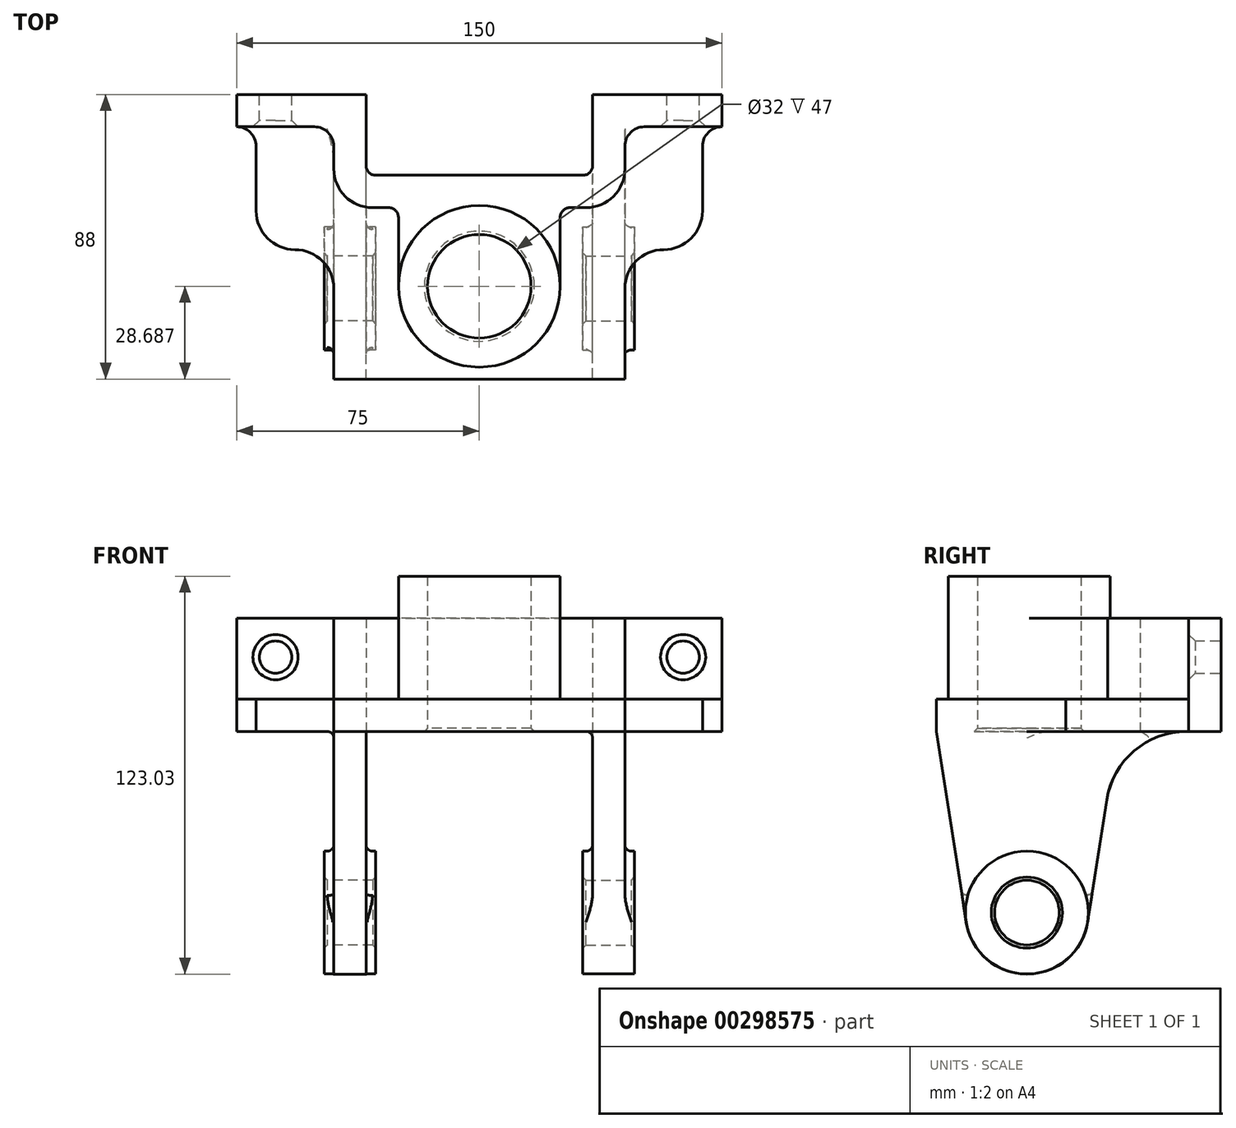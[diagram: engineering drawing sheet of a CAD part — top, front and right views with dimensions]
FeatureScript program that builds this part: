
annotation { "Feature Type Name" : "Feature", "Feature Type Description" : "" }
export const myFeature = defineFeature(function(context is Context, id is Id, definition is map)
    precondition{}
    {
        {
            var Q0;
            Q0=qCreatedBy(makeId("Top.planeOp"),FACE);
            var sketch = newSketch(context, id + "F0", { "sketchPlane" : qUnion([Q0])});
            skLineSegment(sketch, "E0", {"start": v(0, 0) * mm, "end": v(32, 0) * mm});
            skLineSegment(sketch, "E1", {"start": v(35, 3) * mm, "end": v(35, 25) * mm});
            skLineSegment(sketch, "E2", {"start": v(35, 25) * mm, "end": v(75, 25) * mm});
            skLineSegment(sketch, "E3", {"start": v(75, 25) * mm, "end": v(75, 15) * mm});
            skLineSegment(sketch, "E4", {"start": v(75, 15) * mm, "end": v(51, 15) * mm});
            skLineSegment(sketch, "E5", {"start": v(45, 9) * mm, "end": v(45, 2) * mm});
            skLineSegment(sketch, "E6", {"start": v(33, -10) * mm, "end": v(25, -10) * mm});
            skLineSegment(sketch, "E7", {"start": v(25, -10) * mm, "end": v(25, -34.31) * mm});
            skArc(sketch, "E8", {"start": v(0, -59.31) * mm, "mid": v(17.68, -52) * mm, "end": v(25, -34.31) * mm});
            skLineSegment(sketch, "E9", {"start": v(0, 0) * mm, "end": v(0, -59.31) * mm});
            skCircle(sketch, "E10", {"center": v(0, -34.31) * mm, "radius": 16 * mm});
            skPoint(sketch, "E11.visualSharp", {"position": v(-35, 0) * mm});
            skPoint(sketch, "E12.visualSharp", {"position": v(35, 0) * mm});
            skArc(sketch, "E12.filletArc", {"start": v(32, 0) * mm, "mid": v(34.12, 0.88) * mm, "end": v(35, 3) * mm});
            skPoint(sketch, "E13.visualSharp", {"position": v(45, -10) * mm});
            skArc(sketch, "E13.filletArc", {"start": v(33, -10) * mm, "mid": v(41.49, -6.49) * mm, "end": v(45, 2) * mm});
            skPoint(sketch, "E14.visualSharp", {"position": v(45, 15) * mm});
            skArc(sketch, "E14.filletArc", {"start": v(51, 15) * mm, "mid": v(46.76, 13.24) * mm, "end": v(45, 9) * mm});
            skPoint(sketch, "E15.MirrorCS.start.orphan", {"position": v(0, 0) * mm});
            skPoint(sketch, "E16.MirrorCS.end.orphan", {"position": v(-35, 25) * mm});
            skPoint(sketch, "E17.MirrorCS.end.orphan", {"position": v(-75, 25) * mm});
            skPoint(sketch, "E18.MirrorCS.end.orphan", {"position": v(-75, 15) * mm});
            skPoint(sketch, "E19.MirrorCS.end.orphan", {"position": v(-45, 15) * mm});
            skPoint(sketch, "E20.MirrorCS.end.orphan", {"position": v(-25, -10) * mm});
            skPoint(sketch, "E21.MirrorCS.end.orphan", {"position": v(-25, -34.31) * mm});
            skPoint(sketch, "E22.MirrorCS.start.orphan", {"position": v(0, -59.31) * mm});
            skLineSegment(sketch, "E23.MirrorCS", {"start": v(0, 0) * mm, "end": v(-32, 0) * mm});
            skArc(sketch, "E24.MirrorCS", {"start": v(-32, 0) * mm, "mid": v(-34.12, 0.88) * mm, "end": v(-35, 3) * mm});
            skLineSegment(sketch, "E25.MirrorCS", {"start": v(-35, 3) * mm, "end": v(-35, 25) * mm});
            skLineSegment(sketch, "E26.MirrorCS", {"start": v(-35, 25) * mm, "end": v(-75, 25) * mm});
            skLineSegment(sketch, "E27.MirrorCS", {"start": v(-75, 25) * mm, "end": v(-75, 15) * mm});
            skArc(sketch, "E28.MirrorCS", {"start": v(-51, 15) * mm, "mid": v(-46.76, 13.24) * mm, "end": v(-45, 9) * mm});
            skLineSegment(sketch, "E29.MirrorCS", {"start": v(-45, 9) * mm, "end": v(-45, 2) * mm});
            skArc(sketch, "E30.MirrorCS", {"start": v(-33, -10) * mm, "mid": v(-41.49, -6.49) * mm, "end": v(-45, 2) * mm});
            skLineSegment(sketch, "E31.MirrorCS", {"start": v(-33, -10) * mm, "end": v(-25, -10) * mm});
            skLineSegment(sketch, "E32.MirrorCS", {"start": v(-25, -10) * mm, "end": v(-25, -34.31) * mm});
            skArc(sketch, "E33.MirrorCS", {"start": v(0, -59.31) * mm, "mid": v(-17.68, -52) * mm, "end": v(-25, -34.31) * mm});
            skLineSegment(sketch, "E34", {"start": v(-51, 15) * mm, "end": v(-75, 15) * mm});
            skSolve(sketch);
        }
        {
            var Q0;
            Q0 = qSketchRegion(id + "F0", true);
            extrude(context, id + "F1", {"entities" : qUnion([Q0]), "depth" : 25 * mm});
        }
        {
            var Q0;
            Q0=makeQuery(id+"F1.opExtrude","CAP_FACE",FACE,{"disambiguationData":[OSD([sQuery(id+"F0.wireOp",EDGE,"E0"),sQuery(id+"F0.wireOp",EDGE,"E1"),sQuery(id+"F0.wireOp",EDGE,"E2"),sQuery(id+"F0.wireOp",EDGE,"E3"),sQuery(id+"F0.wireOp",EDGE,"E4"),sQuery(id+"F0.wireOp",EDGE,"E5"),sQuery(id+"F0.wireOp",EDGE,"E6"),sQuery(id+"F0.wireOp",EDGE,"E7"),sQuery(id+"F0.wireOp",EDGE,"E8"),sQuery(id+"F0.wireOp",EDGE,"E10"),sQuery(id+"F0.wireOp",EDGE,"E12.filletArc"),sQuery(id+"F0.wireOp",EDGE,"E13.filletArc"),sQuery(id+"F0.wireOp",EDGE,"E14.filletArc"),sQuery(id+"F0.wireOp",EDGE,"E23.MirrorCS"),sQuery(id+"F0.wireOp",EDGE,"E24.MirrorCS"),sQuery(id+"F0.wireOp",EDGE,"E25.MirrorCS"),sQuery(id+"F0.wireOp",EDGE,"E26.MirrorCS"),sQuery(id+"F0.wireOp",EDGE,"E27.MirrorCS"),sQuery(id+"F0.wireOp",EDGE,"24cce044-26b0-4711-a261-53512b01c6400.MirrorCS"),sQuery(id+"F0.wireOp",EDGE,"E28.MirrorCS"),sQuery(id+"F0.wireOp",EDGE,"E29.MirrorCS"),sQuery(id+"F0.wireOp",EDGE,"E30.MirrorCS"),sQuery(id+"F0.wireOp",EDGE,"E31.MirrorCS"),sQuery(id+"F0.wireOp",EDGE,"E32.MirrorCS"),sQuery(id+"F0.wireOp",EDGE,"E33.MirrorCS")])],"isStart":false});
            var sketch = newSketch(context, id + "F2", { "sketchPlane" : qUnion([Q0])});
            skCircle(sketch, "E35", {"center": v(0, -34.31) * mm, "radius": 25 * mm});
            skSolve(sketch);
        }
        {
            var Q0;
            Q0 = qSketchRegion(id + "F2", true);
            extrude(context, id + "F3", {"entities" : qUnion([Q0]), "operationType" : NewBodyOperationType.ADD, "depth" : 13 * mm});
        }
        {
            var Q0;
            Q0=makeQuery(id+"F3.opExtrude","CAP_FACE",FACE,{"disambiguationData":[OSD([sQuery(id+"F2.wireOp",EDGE,"E35")])],"isStart":false});
            var sketch = newSketch(context, id + "F4", { "sketchPlane" : qUnion([Q0])});
            skCircle(sketch, "E36", {"center": v(0, -34.31) * mm, "radius": 16 * mm});
            skSolve(sketch);
        }
        {
            var Q0;
            Q0 = qSketchRegion(id + "F4", true);
            extrude(context, id + "F5", {"entities" : qUnion([Q0]), "operationType" : NewBodyOperationType.REMOVE, "endBound" : BoundingType.THROUGH_ALL, "oppositeDirection" : true, "depth" : 25 * mm});
        }
        {
            var Q0;
            Q0=makeQuery(id+"F1.opExtrude","SWEPT_EDGE",EDGE,{"disambiguationData":[OSD([sQuery(id+"F0.wireOp",EDGE,"E6"),sQuery(id+"F0.wireOp",EDGE,"E7")])]});
            var Q1;
            Q1=makeQuery(id+"F1.opExtrude","SWEPT_EDGE",EDGE,{"disambiguationData":[OSD([sQuery(id+"F0.wireOp",EDGE,"E31.MirrorCS"),sQuery(id+"F0.wireOp",EDGE,"E32.MirrorCS")])]});
            fillet(context, id + "F6", {"entities" : qUnion([Q0, Q1]), "radius" : 3 * mm, "tangentPropagation" : true, "allowEdgeOverflow" : false});
        }
        {
            var Q0;
            Q0=qCreatedBy(makeId("Top.planeOp"),FACE);
            var sketch = newSketch(context, id + "F7", { "sketchPlane" : qUnion([Q0])});
            skPoint(sketch, "E37.0", {"position": v(-75, 20) * mm});
            skPoint(sketch, "E38.0", {"position": v(-55, 25) * mm});
            skLineSegment(sketch, "E39.0", {"start": v(-35, 3) * mm, "end": v(-35, 25) * mm});
            skPoint(sketch, "E40.0", {"position": v(-34.12, 0.88) * mm});
            skLineSegment(sketch, "E41.0", {"start": v(-32, 0) * mm, "end": v(32, 0) * mm});
            skPoint(sketch, "E42.0", {"position": v(34.12, 0.88) * mm});
            skLineSegment(sketch, "E43.0", {"start": v(35, 3) * mm, "end": v(35, 25) * mm});
            skLineSegment(sketch, "E44.0", {"start": v(35, 25) * mm, "end": v(75, 25) * mm});
            skLineSegment(sketch, "E45.0.0", {"start": v(75, 15) * mm, "end": v(75, 25) * mm});
            skLineSegment(sketch, "E45.0.2", {"start": v(75, 25) * mm, "end": v(75, 15) * mm});
            skLineSegment(sketch, "E46.0", {"start": v(-35, 25) * mm, "end": v(-75, 25) * mm});
            skArc(sketch, "E47.0", {"start": v(32, 0) * mm, "mid": v(34.12, 0.88) * mm, "end": v(35, 3) * mm});
            skArc(sketch, "E48.0", {"start": v(-32, 0) * mm, "mid": v(-34.12, 0.88) * mm, "end": v(-35, 3) * mm});
            skPoint(sketch, "E49.0.end.orphan", {"position": v(-75, 15) * mm});
            skPoint(sketch, "E49.0.start.orphan", {"position": v(-51, 15) * mm});
            skLineSegment(sketch, "E50.0", {"start": v(-75, 25) * mm, "end": v(-75, 15) * mm});
            skLineSegment(sketch, "E51", {"start": v(75, 15) * mm, "end": v(75, 15) * mm});
            skLineSegment(sketch, "E52", {"start": v(69, 9) * mm, "end": v(69, -11) * mm});
            skLineSegment(sketch, "E53", {"start": v(57, -23) * mm, "end": v(57, -23) * mm});
            skLineSegment(sketch, "E54", {"start": v(45, -35) * mm, "end": v(45, -63) * mm});
            skLineSegment(sketch, "E55", {"start": v(45, -63) * mm, "end": v(-45, -63) * mm});
            skLineSegment(sketch, "E56", {"start": v(-45, -63) * mm, "end": v(-45, -35) * mm});
            skLineSegment(sketch, "E57", {"start": v(-57, -23) * mm, "end": v(-57, -23) * mm});
            skLineSegment(sketch, "E58", {"start": v(-69, -11) * mm, "end": v(-69, 9) * mm});
            skLineSegment(sketch, "E59", {"start": v(-75, 15) * mm, "end": v(-75, 15) * mm});
            skCircle(sketch, "E60.0", {"center": v(0, -34.31) * mm, "radius": 16 * mm});
            skPoint(sketch, "E61.visualSharp", {"position": v(69, 15) * mm});
            skArc(sketch, "E61.filletArc", {"start": v(75, 15) * mm, "mid": v(70.76, 13.24) * mm, "end": v(69, 9) * mm});
            skPoint(sketch, "E62.visualSharp", {"position": v(69, -23) * mm});
            skArc(sketch, "E62.filletArc", {"start": v(57, -23) * mm, "mid": v(65.49, -19.49) * mm, "end": v(69, -11) * mm});
            skPoint(sketch, "E63.visualSharp", {"position": v(45, -23) * mm});
            skArc(sketch, "E63.filletArc", {"start": v(57, -23) * mm, "mid": v(48.51, -26.51) * mm, "end": v(45, -35) * mm});
            skPoint(sketch, "E64.visualSharp", {"position": v(-45, -23) * mm});
            skArc(sketch, "E64.filletArc", {"start": v(-45, -35) * mm, "mid": v(-48.51, -26.51) * mm, "end": v(-57, -23) * mm});
            skPoint(sketch, "E65.visualSharp", {"position": v(-69, -23) * mm});
            skArc(sketch, "E65.filletArc", {"start": v(-69, -11) * mm, "mid": v(-65.49, -19.49) * mm, "end": v(-57, -23) * mm});
            skPoint(sketch, "E66.visualSharp", {"position": v(-69, 15) * mm});
            skArc(sketch, "E66.filletArc", {"start": v(-69, 9) * mm, "mid": v(-70.76, 13.24) * mm, "end": v(-75, 15) * mm});
            skSolve(sketch);
        }
        {
            var Q0;
            Q0 = qSketchRegion(id + "F7", true);
            extrude(context, id + "F8", {"entities" : qUnion([Q0]), "operationType" : NewBodyOperationType.ADD, "oppositeDirection" : true, "depth" : 10 * mm});
        }
        {
            var Q0;
            Q0=makeQuery(id+"F8.opExtrude","SWEPT_FACE",FACE,{"disambiguationData":[OSD([sQuery(id+"F7.wireOp",EDGE,"E54")])]});
            cPlane(context, id + "F9", {"entities" : qUnion([Q0]), "cplaneType" : CPlaneType.OFFSET, "offset" : 0 * mm, "width" : 150 * mm, "height" : 150 * mm});
        }
        {
            var Q0;
            Q0=qCreatedBy(id+"F9.planeOp",FACE);
            var sketch = newSketch(context, id + "F10", { "sketchPlane" : qUnion([Q0])});
            skCircle(sketch, "E67", {"center": v(-35, -66) * mm, "radius": 19 * mm});
            skCircle(sketch, "E68", {"center": v(-35, -66) * mm, "radius": 10 * mm});
            skLineSegment(sketch, "E69", {"start": v(-63, -10) * mm, "end": v(-53.77, -68.94) * mm});
            skLineSegment(sketch, "E70.MirrorCS", {"start": v(-10.3, -31.13) * mm, "end": v(-16.23, -68.94) * mm});
            skPoint(sketch, "E71.visualSharp", {"position": v(-7, -10) * mm});
            skArc(sketch, "E71.filletArc", {"start": v(14.4, -10) * mm, "mid": v(-1.86, -16) * mm, "end": v(-10.3, -31.13) * mm});
            skLineSegment(sketch, "E72", {"start": v(-63, -10) * mm, "end": v(14.4, -10) * mm});
            skSolve(sketch);
        }
        {
            var Q0;
            Q0 = qSketchRegion(id + "F10", true);
            extrude(context, id + "F11", {"entities" : qUnion([Q0]), "operationType" : NewBodyOperationType.ADD, "oppositeDirection" : true, "depth" : 10 * mm});
        }
        {
            var Q0;
            Q0=makeQuery(id+"F8.opExtrude","SWEPT_FACE",FACE,{"disambiguationData":[OSD([sQuery(id+"F7.wireOp",EDGE,"E56")])]});
            cPlane(context, id + "F12", {"entities" : qUnion([Q0]), "cplaneType" : CPlaneType.OFFSET, "offset" : 0 * mm, "width" : 150 * mm, "height" : 150 * mm});
        }
        {
            var Q0;
            Q0=qCreatedBy(id+"F12.planeOp",FACE);
            var sketch = newSketch(context, id + "F13", { "sketchPlane" : qUnion([Q0])});
            skLineSegment(sketch, "E73.0", {"start": v(63, -10) * mm, "end": v(35, -10) * mm});
            skCircle(sketch, "E74", {"center": v(35, -66) * mm, "radius": 19.03 * mm});
            skCircle(sketch, "E75", {"center": v(35, -66) * mm, "radius": 10 * mm});
            skLineSegment(sketch, "E76", {"start": v(63, -10) * mm, "end": v(53.8, -68.93) * mm});
            skLineSegment(sketch, "E77.MirrorCS", {"start": v(10.3, -31.15) * mm, "end": v(16.2, -68.93) * mm});
            skPoint(sketch, "E78.visualSharp", {"position": v(7, -10) * mm});
            skArc(sketch, "E78.filletArc", {"start": v(10.3, -31.15) * mm, "mid": v(1.86, -16) * mm, "end": v(-14.4, -10) * mm});
            skLineSegment(sketch, "E79", {"start": v(63, -10) * mm, "end": v(-14.4, -10) * mm});
            skSolve(sketch);
        }
        {
            var Q0;
            Q0 = qSketchRegion(id + "F13", true);
            extrude(context, id + "F14", {"entities" : qUnion([Q0]), "operationType" : NewBodyOperationType.ADD, "oppositeDirection" : true, "depth" : 10 * mm});
        }
        {
            var Q0;
            Q0=makeQuery(id+"F11.boolean.opBoolean","MERGE",FACE,{"derivedFrom":[makeQuery(id+"F8.opExtrude","SWEPT_FACE",FACE,{"disambiguationData":[OSD([sQuery(id+"F7.wireOp",EDGE,"E54")])]}),makeQuery(id+"F11.opExtrude","CAP_FACE",FACE,{"disambiguationData":[OSD([sQuery(id+"F10.wireOp",EDGE,"E67"),sQuery(id+"F10.wireOp",EDGE,"E68"),sQuery(id+"F10.wireOp",EDGE,"E69"),sQuery(id+"F10.wireOp",EDGE,"E70.MirrorCS"),sQuery(id+"F10.wireOp",EDGE,"E71.filletArc"),sQuery(id+"F10.wireOp",EDGE,"E72")])],"isStart":true})]});
            cPlane(context, id + "F15", {"entities" : qUnion([Q0]), "cplaneType" : CPlaneType.OFFSET, "offset" : 3 * mm, "width" : 150 * mm, "height" : 150 * mm});
        }
        {
            var Q0;
            Q0=qCreatedBy(id+"F15.planeOp",FACE);
            var sketch = newSketch(context, id + "F16", { "sketchPlane" : qUnion([Q0])});
            skCircle(sketch, "E80.0", {"center": v(-35, -66) * mm, "radius": 10 * mm});
            skCircle(sketch, "E81", {"center": v(-35, -66) * mm, "radius": 19 * mm});
            skSolve(sketch);
        }
        {
            var Q0;
            Q0=makeQuery(id+"F16.imprint","IMPRINT",FACE,{"disambiguationData":[TD([[makeQuery(id+"F16.imprint","IMPRINT",EDGE,{"derivedFrom":sQuery(id+"F16.wireOp",EDGE,"E80.0")}),-1.0]])]});
            extrude(context, id + "F17", {"entities" : qUnion([Q0]), "operationType" : NewBodyOperationType.ADD, "oppositeDirection" : true, "depth" : 16 * mm});
        }
        {
            var Q0;
            Q0=makeQuery(id+"F14.boolean.opBoolean","MERGE",FACE,{"derivedFrom":[makeQuery(id+"F8.opExtrude","SWEPT_FACE",FACE,{"disambiguationData":[OSD([sQuery(id+"F7.wireOp",EDGE,"E56")])]}),makeQuery(id+"F14.opExtrude","CAP_FACE",FACE,{"disambiguationData":[OSD([sQuery(id+"F13.wireOp",EDGE,"E74"),sQuery(id+"F13.wireOp",EDGE,"E75"),sQuery(id+"F13.wireOp",EDGE,"E76"),sQuery(id+"F13.wireOp",EDGE,"E77.MirrorCS"),sQuery(id+"F13.wireOp",EDGE,"E78.filletArc"),sQuery(id+"F13.wireOp",EDGE,"E79")])],"isStart":true})]});
            cPlane(context, id + "F18", {"entities" : qUnion([Q0]), "cplaneType" : CPlaneType.OFFSET, "offset" : 3 * mm, "width" : 150 * mm, "height" : 150 * mm});
        }
        {
            var Q0;
            Q0=qCreatedBy(id+"F18.planeOp",FACE);
            var sketch = newSketch(context, id + "F19", { "sketchPlane" : qUnion([Q0])});
            skCircle(sketch, "E82.0", {"center": v(35, -66) * mm, "radius": 10 * mm});
            skCircle(sketch, "E83", {"center": v(35, -66) * mm, "radius": 19 * mm});
            skSolve(sketch);
        }
        {
            var Q0;
            Q0 = qSketchRegion(id + "F19", true);
            extrude(context, id + "F20", {"entities" : qUnion([Q0]), "operationType" : NewBodyOperationType.ADD, "oppositeDirection" : true, "depth" : 16 * mm});
        }
        {
            var Q0;
            Q0=makeQuery(id+"F8.boolean.opBoolean","MERGE",FACE,{"derivedFrom":[makeQuery(id+"F1.opExtrude","SWEPT_FACE",FACE,{"disambiguationData":[OSD([sQuery(id+"F0.wireOp",EDGE,"E2")])]}),makeQuery(id+"F8.opExtrude","SWEPT_FACE",FACE,{"disambiguationData":[OSD([sQuery(id+"F7.wireOp",EDGE,"E44.0")])]})]});
            cPlane(context, id + "F21", {"entities" : qUnion([Q0]), "cplaneType" : CPlaneType.OFFSET, "offset" : 0 * mm, "width" : 150 * mm, "height" : 150 * mm});
        }
        {
            var Q0;
            Q0=qCreatedBy(id+"F21.planeOp",FACE);
            var sketch = newSketch(context, id + "F22", { "sketchPlane" : qUnion([Q0])});
            skCircle(sketch, "E84", {"center": v(-63, 13) * mm, "radius": 5 * mm});
            skCircle(sketch, "E85.MirrorC", {"center": v(63, 13) * mm, "radius": 5 * mm});
            skSolve(sketch);
        }
        {
            var Q0;
            Q0 = qSketchRegion(id + "F22", true);
            extrude(context, id + "F23", {"entities" : qUnion([Q0]), "operationType" : NewBodyOperationType.REMOVE, "oppositeDirection" : true, "depth" : 25 * mm});
        }
        {
            var Q0;
            Q0=makeQuery(id+"F23.boolean.opBoolean","INTERSECT",EDGE,{"derivedFrom":[makeQuery(id+"F1.opExtrude","SWEPT_FACE",FACE,{"disambiguationData":[OSD([sQuery(id+"F0.wireOp",EDGE,"E34")])]}),makeQuery(id+"F23.opExtrude","SWEPT_FACE",FACE,{"disambiguationData":[OSD([sQuery(id+"F22.wireOp",EDGE,"E85.MirrorC")])]})]});
            var Q1;
            Q1=makeQuery(id+"F23.boolean.opBoolean","INTERSECT",EDGE,{"derivedFrom":[makeQuery(id+"F1.opExtrude","SWEPT_FACE",FACE,{"disambiguationData":[OSD([sQuery(id+"F0.wireOp",EDGE,"E4")])]}),makeQuery(id+"F23.opExtrude","SWEPT_FACE",FACE,{"disambiguationData":[OSD([sQuery(id+"F22.wireOp",EDGE,"E84")])]})]});
            chamfer(context, id + "F24", {"entities" : qUnion([Q0, Q1]), "width" : 2 * mm, "tangentPropagation" : true});
        }
        {
            var Q0;
            Q0=makeQuery(id+"F5.boolean.opBoolean","COPY",EDGE,{"derivedFrom":makeQuery(id+"F5.opExtrude","CAP_EDGE",EDGE,{"disambiguationData":[OSD([sQuery(id+"F4.wireOp",EDGE,"E36")])],"isStart":true})});
            var Q1;
            Q1=makeQuery(id+"F20.opExtrude","CAP_EDGE",EDGE,{"disambiguationData":[OSD([sQuery(id+"F19.wireOp",EDGE,"E82.0")])],"isStart":true});
            var Q2;
            Q2=makeQuery(id+"F20.opExtrude","CAP_EDGE",EDGE,{"disambiguationData":[OSD([sQuery(id+"F19.wireOp",EDGE,"E82.0")])],"isStart":false});
            var Q3;
            Q3=makeQuery(id+"F8.opExtrude","CAP_EDGE",EDGE,{"disambiguationData":[OSD([sQuery(id+"F7.wireOp",EDGE,"E60.0")])],"isStart":false});
            var Q4;
            Q4=makeQuery(id+"F17.opExtrude","CAP_EDGE",EDGE,{"disambiguationData":[OSD([sQuery(id+"F16.wireOp",EDGE,"E80.0")])],"isStart":false});
            var Q5;
            Q5=makeQuery(id+"F17.opExtrude","CAP_EDGE",EDGE,{"disambiguationData":[OSD([sQuery(id+"F16.wireOp",EDGE,"E80.0")])],"isStart":true});
            chamfer(context, id + "F25", {"entities" : qUnion([Q0, Q1, Q2, Q3, Q4, Q5]), "width" : 1 * mm, "tangentPropagation" : true});
        }
        {
            var Q0;
            Q0=makeQuery(id+"F1.opExtrude","CAP_EDGE",EDGE,{"disambiguationData":[OSD([sQuery(id+"F0.wireOp",EDGE,"E13.filletArc")])],"isStart":true});
            var Q1;
            Q1=makeQuery(id+"F3.opExtrude","CAP_EDGE",EDGE,{"disambiguationData":[OSD([sQuery(id+"F2.wireOp",EDGE,"E35")])],"isStart":true});
            var Q2;
            Q2=makeQuery(id+"F11.opExtrude","CAP_EDGE",EDGE,{"disambiguationData":[OSD([sQuery(id+"F10.wireOp",EDGE,"E72")])],"isStart":true});
            var Q3;
            Q3=makeQuery(id+"F11.opExtrude","CAP_EDGE",EDGE,{"disambiguationData":[OSD([sQuery(id+"F10.wireOp",EDGE,"E72")])],"isStart":false});
            var Q4;
            Q4=makeQuery(id+"F14.opExtrude","CAP_EDGE",EDGE,{"disambiguationData":[OSD([sQuery(id+"F13.wireOp",EDGE,"E79")])],"isStart":false});
            var Q5;
            Q5=makeQuery(id+"F14.opExtrude","CAP_EDGE",EDGE,{"disambiguationData":[OSD([sQuery(id+"F13.wireOp",EDGE,"E79")])],"isStart":true});
            var Q6;
            Q6=makeQuery(id+"F17.boolean.opBoolean","INTERSECT",EDGE,{"derivedFrom":[makeQuery(id+"F11.boolean.opBoolean","MERGE",FACE,{"derivedFrom":[makeQuery(id+"F8.boolean.opBoolean","MERGE",FACE,{"derivedFrom":[makeQuery(id+"F1.opExtrude","SWEPT_FACE",FACE,{"disambiguationData":[OSD([sQuery(id+"F0.wireOp",EDGE,"E1")])]}),makeQuery(id+"F8.opExtrude","SWEPT_FACE",FACE,{"disambiguationData":[OSD([sQuery(id+"F7.wireOp",EDGE,"E43.0")])]})]}),makeQuery(id+"F11.opExtrude","CAP_FACE",FACE,{"disambiguationData":[OSD([sQuery(id+"F10.wireOp",EDGE,"E67"),sQuery(id+"F10.wireOp",EDGE,"E68"),sQuery(id+"F10.wireOp",EDGE,"E69"),sQuery(id+"F10.wireOp",EDGE,"E70.MirrorCS"),sQuery(id+"F10.wireOp",EDGE,"E71.filletArc"),sQuery(id+"F10.wireOp",EDGE,"E72")])],"isStart":false})]}),makeQuery(id+"F17.opExtrude","SWEPT_FACE",FACE,{"disambiguationData":[OSD([sQuery(id+"F16.wireOp",EDGE,"E81")])]})]});
            var Q7;
            Q7=makeQuery(id+"F20.boolean.opBoolean","INTERSECT",EDGE,{"derivedFrom":[makeQuery(id+"F14.boolean.opBoolean","MERGE",FACE,{"derivedFrom":[makeQuery(id+"F8.opExtrude","SWEPT_FACE",FACE,{"disambiguationData":[OSD([sQuery(id+"F7.wireOp",EDGE,"E56")])]}),makeQuery(id+"F14.opExtrude","CAP_FACE",FACE,{"disambiguationData":[OSD([sQuery(id+"F13.wireOp",EDGE,"E74"),sQuery(id+"F13.wireOp",EDGE,"E75"),sQuery(id+"F13.wireOp",EDGE,"E76"),sQuery(id+"F13.wireOp",EDGE,"E77.MirrorCS"),sQuery(id+"F13.wireOp",EDGE,"E78.filletArc"),sQuery(id+"F13.wireOp",EDGE,"E79")])],"isStart":true})]}),makeQuery(id+"F20.opExtrude","SWEPT_FACE",FACE,{"disambiguationData":[OSD([sQuery(id+"F19.wireOp",EDGE,"E83")])]})]});
            var Q8;
            Q8=makeQuery(id+"F20.boolean.opBoolean","INTERSECT",EDGE,{"derivedFrom":[makeQuery(id+"F14.boolean.opBoolean","MERGE",FACE,{"derivedFrom":[makeQuery(id+"F8.boolean.opBoolean","MERGE",FACE,{"derivedFrom":[makeQuery(id+"F1.opExtrude","SWEPT_FACE",FACE,{"disambiguationData":[OSD([sQuery(id+"F0.wireOp",EDGE,"E25.MirrorCS")])]}),makeQuery(id+"F8.opExtrude","SWEPT_FACE",FACE,{"disambiguationData":[OSD([sQuery(id+"F7.wireOp",EDGE,"E39.0")])]})]}),makeQuery(id+"F14.opExtrude","CAP_FACE",FACE,{"disambiguationData":[OSD([sQuery(id+"F13.wireOp",EDGE,"E74"),sQuery(id+"F13.wireOp",EDGE,"E75"),sQuery(id+"F13.wireOp",EDGE,"E76"),sQuery(id+"F13.wireOp",EDGE,"E77.MirrorCS"),sQuery(id+"F13.wireOp",EDGE,"E78.filletArc"),sQuery(id+"F13.wireOp",EDGE,"E79")])],"isStart":false})]}),makeQuery(id+"F20.opExtrude","SWEPT_FACE",FACE,{"disambiguationData":[OSD([sQuery(id+"F19.wireOp",EDGE,"E83")])]})]});
            var Q9;
            Q9=makeQuery(id+"F17.boolean.opBoolean","INTERSECT",EDGE,{"derivedFrom":[makeQuery(id+"F11.boolean.opBoolean","MERGE",FACE,{"derivedFrom":[makeQuery(id+"F8.opExtrude","SWEPT_FACE",FACE,{"disambiguationData":[OSD([sQuery(id+"F7.wireOp",EDGE,"E54")])]}),makeQuery(id+"F11.opExtrude","CAP_FACE",FACE,{"disambiguationData":[OSD([sQuery(id+"F10.wireOp",EDGE,"E67"),sQuery(id+"F10.wireOp",EDGE,"E68"),sQuery(id+"F10.wireOp",EDGE,"E69"),sQuery(id+"F10.wireOp",EDGE,"E70.MirrorCS"),sQuery(id+"F10.wireOp",EDGE,"E71.filletArc"),sQuery(id+"F10.wireOp",EDGE,"E72")])],"isStart":true})]}),makeQuery(id+"F17.opExtrude","SWEPT_FACE",FACE,{"disambiguationData":[OSD([sQuery(id+"F16.wireOp",EDGE,"E81")])]})]});
            fillet(context, id + "F26", {"entities" : qUnion([Q0, Q1, Q2, Q3, Q4, Q5, Q6, Q7, Q8, Q9]), "radius" : 2 * mm, "tangentPropagation" : true, "allowEdgeOverflow" : false});
        }
    });
